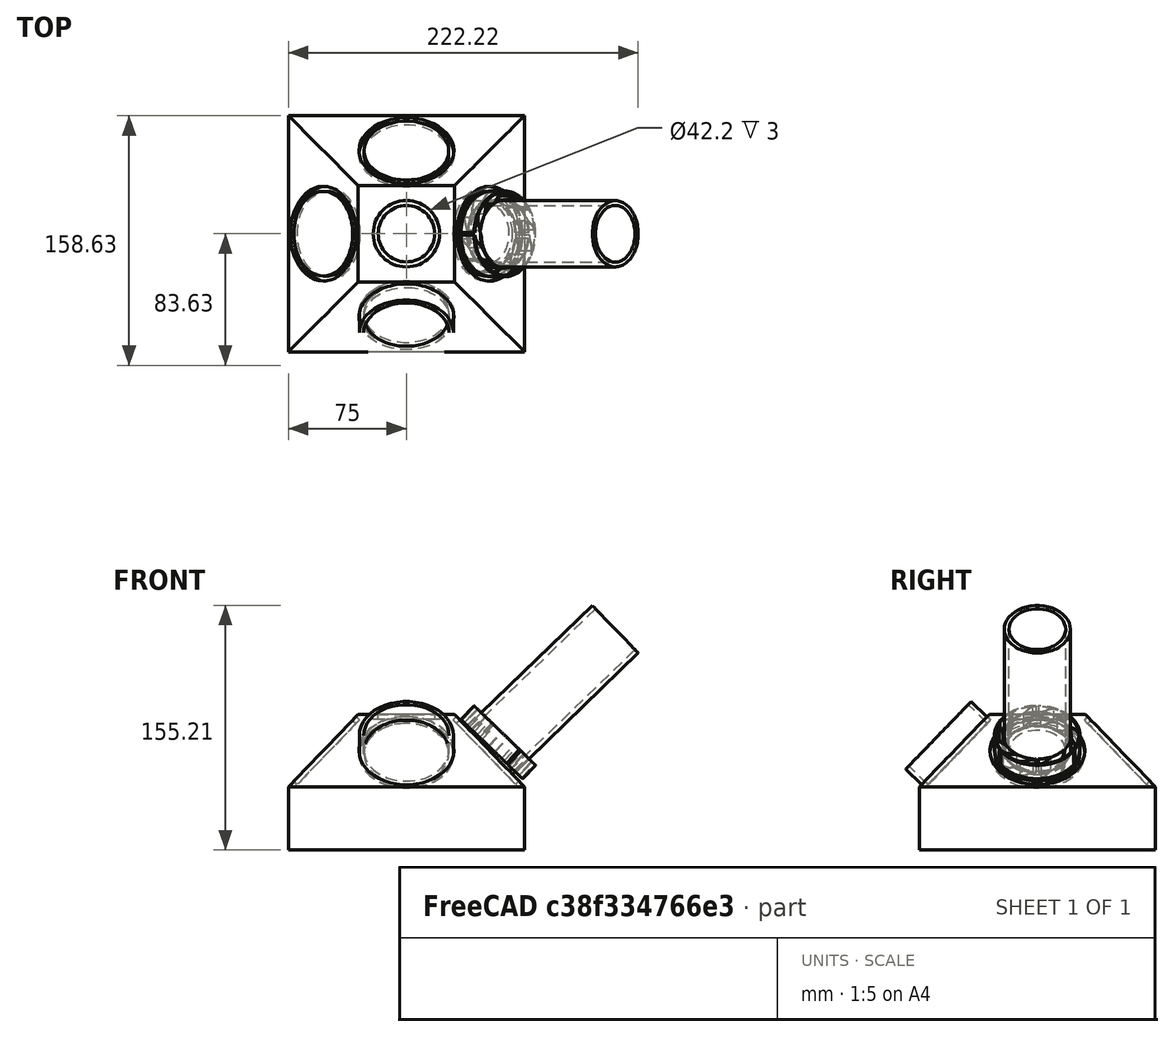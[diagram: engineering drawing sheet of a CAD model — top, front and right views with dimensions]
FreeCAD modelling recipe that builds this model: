
FCSTD DOCUMENT  (FreeCAD 0.21R32867 (Git))
Label: pipestar
License: All rights reserved
LicenseURL: https://en.wikipedia.org/wiki/All_rights_reserved
objects: Sketcher::SketchObject×7, Part::FeaturePython×5, PartDesign::Pocket×4, PartDesign::PolarPattern×4, Mesh::Feature×3, PartDesign::Pad×3, PartDesign::Body×2, Spreadsheet::Sheet×1, App::Part×1
note: 31 computed .brp shape members not serialized (recipe doc carries the construction recipe); baked Part::Feature solids carry a one-line shape summary decoded from their .brp

FEATURE [Mesh::Feature] Mesh
FEATURE [Mesh::Feature] Mesh001
FEATURE [Sketcher::SketchObject] Sketch  label="base1Sketch"
  FullyConstrained = true
  MapMode = 5
  Support = -> [XY_Plane]
  expr: Constraints[9] = <<params>>.baseWidth
  sketch-geometry (4):
    g0: LineSegment StartX=-75 StartY=75 StartZ=0 EndX=75 EndY=75 EndZ=0
    g1: LineSegment StartX=75 StartY=75 StartZ=0 EndX=75 EndY=-75 EndZ=0
    g2: LineSegment StartX=75 StartY=-75 StartZ=0 EndX=-75 EndY=-75 EndZ=0
    g3: LineSegment StartX=-75 StartY=-75 StartZ=0 EndX=-75 EndY=75 EndZ=0
  constraints (11):
    c: Coincident(g0,g1)
    c: Coincident(g1,g2)
    c: Coincident(g2,g3)
    c: Coincident(g3,g0)
    c: Horizontal(g0)
    c: Horizontal(g2)
    c: Vertical(g1)
    c: Vertical(g3)
    c: Equal(g2,g1)
    c: DistanceX(g2,g2) = 150
    c: Symmetric(g1,g0,g-1)
FEATURE [PartDesign::Pad] Pad  label="base1"
  Direction = (0,0,1)
  Length = 40
  Length2 = 10
  Profile = -> Sketch
  ReferenceAxis = -> Sketch [N_Axis]
  Type = 0
  expr: Length = <<params>>.baseHeight1
FEATURE [Sketcher::SketchObject] Sketch001  label="base2Sketch"
  FullyConstrained = true
  MapMode = 5
  Placement = pos=(0,0,40) rot=(0,0,1;0rad)
  Support = -> [Pad]
  expr: Constraints[9] = Sketch.Constraints[9]
  sketch-geometry (4):
    g0: LineSegment StartX=-75 StartY=75 StartZ=0 EndX=75 EndY=75 EndZ=0
    g1: LineSegment StartX=75 StartY=75 StartZ=0 EndX=75 EndY=-75 EndZ=0
    g2: LineSegment StartX=75 StartY=-75 StartZ=0 EndX=-75 EndY=-75 EndZ=0
    g3: LineSegment StartX=-75 StartY=-75 StartZ=0 EndX=-75 EndY=75 EndZ=0
  constraints (11):
    c: Coincident(g0,g1)
    c: Coincident(g1,g2)
    c: Coincident(g2,g3)
    c: Coincident(g3,g0)
    c: Horizontal(g0)
    c: Horizontal(g2)
    c: Vertical(g1)
    c: Vertical(g3)
    c: Equal(g2,g1)
    c: DistanceX(g2,g2) = 150
    c: Symmetric(g1,g0,g-1)
FEATURE [PartDesign::Pad] Pad001  label="base2"
  BaseFeature = -> Pad
  Direction = (0,0,1)
  Length = 46
  Length2 = 10
  Profile = -> Sketch001
  ReferenceAxis = -> Sketch001 [N_Axis]
  TaperAngle = -44
  Type = 0
  expr: Length = <<params>>.baseHeight2
  expr: TaperAngle = <<params>>.baseTaperAngel
FEATURE [Sketcher::SketchObject] Sketch002
  ExternalGeometry = -> [Pad001]
  FullyConstrained = true
  MapMode = 45
  Placement = pos=(-3e-15,-55.9042,59.7743) rot=(0.677258,0.677258,0.287479;3.70145rad)
  Support = -> [Pad001]
  sketch-geometry (4):
    g0: Circle CenterX=4.48428 CenterY=0 CenterZ=0 NormalX=0 NormalY=0 NormalZ=1 AngleXU=0 Radius=30.1
    g1: Circle CenterX=4.48428 CenterY=0 CenterZ=0 NormalX=0 NormalY=0 NormalZ=1 AngleXU=0 Radius=26.9
    g2: LineSegment StartX=-27.4895 StartY=0 StartZ=0 EndX=-25.6157 EndY=0 EndZ=0
    g3: LineSegment StartX=34.5843 StartY=0 StartZ=0 EndX=36.458 EndY=0 EndZ=0
  constraints (13):
    c: Diameter(g0) = 60.2
    c: Coincident(g1,g0)
    c: Diameter(g1) = 53.8
    c: PointOnObject(g0,g-1)
    c: PointOnObject(g2,g-4)
    c: PointOnObject(g2,g0)
    c: PointOnObject(g3,g0)
    c: PointOnObject(g3,g-3)
    c: PointOnObject(g3,g-1)
    c: Perpendicular(g0,g3)
    c: PointOnObject(g2,g-1)
    c: Perpendicular(g0,g2)
    c: Equal(g3,g2)
FEATURE [Sketcher::SketchObject] Sketch003
  FullyConstrained = true
  MapMode = 5
  Placement = pos=(0,0,86) rot=(0,0,1;0rad)
  sketch-geometry (2):
    g0: Circle CenterX=0 CenterY=0 CenterZ=0 NormalX=0 NormalY=0 NormalZ=1 AngleXU=0 Radius=21.1
    g1: Circle CenterX=0 CenterY=0 CenterZ=0 NormalX=0 NormalY=0 NormalZ=1 AngleXU=0 Radius=17.9
  constraints (4):
    c: Coincident(g0,g-1)
    c: Diameter(g0) = 42.2
    c: Coincident(g1,g0)
    c: Diameter(g1) = 35.8
FEATURE [PartDesign::Pocket] Pocket  label="tubeSideMountingRecess"
  BaseFeature = -> Pad001
  Direction = (0,-0.71934,0.694658)
  Length = 3
  Length2 = 5
  Profile = -> Sketch002
  ReferenceAxis = -> Sketch002 [N_Axis]
  Reversed = true
  Type = 0
FEATURE [PartDesign::PolarPattern] PolarPattern
  Angle = 360
  Axis = -> Z_Axis
  BaseFeature = -> Pocket
  Occurrences = 4
  Originals = -> [Pocket]
FEATURE [PartDesign::Pocket] Pocket001  label="tubeTopMountingRecess"
  BaseFeature = -> PolarPattern
  Direction = (0,0,-1)
  Length = 3
  Length2 = 5
  Profile = -> Sketch003
  ReferenceAxis = -> Sketch003 [N_Axis]
  Type = 0
FEATURE [PartDesign::Body] Body  label="base"
  Group = -> [Sketch,Pad,Sketch001,Pad001,Sketch002,Sketch003,Pocket,PolarPattern,Pocket001]
  Origin = -> Origin
  Tip = -> Pocket001
FEATURE [Part::FeaturePython] Tube  label="tubeTop"  # WARN: FeaturePython — macro-defined, semantics opaque (R4)
  AttacherType = Attacher::AttachEngine3D
  Height = 111
  InnerRadius = 18
  OuterRadius = 21
  Placement = pos=(0,0,83) rot=(0,0,1;0rad)
FEATURE [Part::FeaturePython] Tube001  label="tubeSide"  # WARN: FeaturePython — macro-defined, semantics opaque (R4)
  AttacherType = Attacher::AttachEngine3D
  Height = 17
  InnerRadius = 27.1
  OuterRadius = 29.9
  Placement = pos=(153,0,0) rot=(1,0,0;0rad)
FEATURE [Part::FeaturePython] Clone  label="Tube1"  # Draft clone (typed FeaturePython)
  AttacherType = Attacher::AttachEngine3D
  Fuse = false
  Objects = -> [Tube001]
  Placement = pos=(0,-50.63,60.92) rot=(1,0,0;0.802851rad)
  Scale = (1,1,1)
FEATURE [Part::FeaturePython] Array  label="arraySide"  # Draft array (typed FeaturePython)
  AlwaysSyncPlacement = false
  Angle = 360
  ArrayType = 1
  Axis = (0,0,1)
  Base = -> Clone
  Center = (0,0,0)
  Count = 4
  ExpandArray = false
  Fuse = false
  IntervalAxis = (0,0,0)
  IntervalX = (50,0,0)
  IntervalY = (0,50,0)
  IntervalZ = (0,0,50)
  NumberCircles = 3
  NumberPolar = 4
  NumberX = 2
  NumberY = 2
  NumberZ = 1
  PlacementList = 4 placements: [(0,-50.63,60.92),(50.63,-1.42109e-14,60.92),(6.20039e-15,50.63,60.92),(-50.63,1.42109e-14,60.92)]
  RadialDistance = 50
  ScaleList = (4) [(1,1,1),(1,1,1),(1,1,1),(1,1,1)]
  Symmetry = 1
  TangentialDistance = 25
FEATURE [Spreadsheet::Sheet] Spreadsheet  label="params"
  cells = A1=baseWidth; B1(baseWidth)==150 mm; A2=baseHeight1; B2(baseHeight1)==40 mm; A3=baseHeight2; B3(baseHeight2)==46 mm; A4=baseTaperAngel; B4(baseTaperAngel)==-44 °; A6=tubeSideOuterRadius; B6(tubeSideOuterRadius)==60 mm; A7=tubeSideInnerRadius; B7(tubeSideInnerRadius)==54 mm; A8=tubeSideHeight; B8(tubeSideHeight)==14 mm; A10=tubeTopOuterRadius; B10(tubeTopOuterRadius)==42 mm; A11=tubeTopInnerRadius; B11(tubeTopInnerRadius)==36 mm; A12=tubeTopHeight; B12(tubeTopHeight)==108 mm; A14=tubeFittingClearance; B14(tubeFittingClearance)==0.4 mm; A15=tubeMountingRecess; B15(tubeMountingRecess)==3 mm
FEATURE [Sketcher::SketchObject] Sketch004
  FullyConstrained = true
  MapMode = 5
  Support = -> [XY_Plane001]
  sketch-geometry (17):
    g0: LineSegment StartX=0 StartY=0 StartZ=0 EndX=18.0133 EndY=10.4 EndZ=0
    g1: LineSegment StartX=18.0133 StartY=10.4 StartZ=0 EndX=18.7061 EndY=10.8 EndZ=0
    g2: LineSegment StartX=18.7061 StartY=10.8 StartZ=0 EndX=22.8631 EndY=13.2 EndZ=0
    g3: LineSegment StartX=22.8631 StartY=13.2 StartZ=0 EndX=23.5559 EndY=13.6 EndZ=0
    g4: ArcOfCircle CenterX=0 CenterY=0 CenterZ=0 NormalX=0 NormalY=0 NormalZ=1 AngleXU=0 Radius=20.8 StartAngle=0 EndAngle=0.523599
    g5: ArcOfCircle CenterX=0 CenterY=0 CenterZ=0 NormalX=0 NormalY=0 NormalZ=1 AngleXU=0 Radius=27.2 StartAngle=0 EndAngle=0.523599
    g6: ArcOfCircle CenterX=0 CenterY=0 CenterZ=0 NormalX=0 NormalY=0 NormalZ=1 AngleXU=0 Radius=21.6 StartAngle=0 EndAngle=0.408252
    g7: ArcOfCircle CenterX=0 CenterY=0 CenterZ=0 NormalX=0 NormalY=0 NormalZ=1 AngleXU=0 Radius=26.4 StartAngle=0.106675 EndAngle=0.523599
    g8: LineSegment StartX=20.8 StartY=0 StartZ=0 EndX=21.6 EndY=0 EndZ=0
    g9: LineSegment StartX=27.2 StartY=0 StartZ=0 EndX=26.4 EndY=0 EndZ=0
    g10: ArcOfCircle CenterX=28.9052 CenterY=16.6884 CenterZ=0 NormalX=0 NormalY=0 NormalZ=1 AngleXU=0 Radius=11.7768 StartAngle=3.66519 EndAngle=4.19208
    g11: LineSegment StartX=19.8248 StartY=8.57531 StartZ=0 EndX=20.1231 EndY=8.84182 EndZ=0
    g12: ArcOfCircle CenterX=19.3431 CenterY=0 CenterZ=0 NormalX=0 NormalY=0 NormalZ=1 AngleXU=0 Radius=7.45691 StartAngle=0.3865 EndAngle=1.05048
    g13: LineSegment StartX=25.8794 StartY=2.6601 StartZ=0 EndX=26.2499 EndY=2.81088 EndZ=0
    g14: ArcOfCircle CenterX=28.9052 CenterY=16.6884 CenterZ=0 NormalX=0 NormalY=0 NormalZ=1 AngleXU=0 Radius=12.1768 StartAngle=3.87079 EndAngle=4.19208
    g15: ArcOfCircle CenterX=19.3431 CenterY=0 CenterZ=0 NormalX=0 NormalY=0 NormalZ=1 AngleXU=0 Radius=7.05691 StartAngle=0 EndAngle=1.05048
    g16: LineSegment StartX=0 StartY=0 StartZ=0 EndX=22.8514 EndY=6.12303 EndZ=0
  constraints (48):
    c: Coincident(g-1,g0)
    c: Coincident(g0,g1)
    c: Coincident(g1,g2)
    c: Coincident(g2,g3)
    c: Parallel(g3,g2)
    c: Parallel(g2,g1)
    c: Parallel(g1,g0)
    c: Equal(g3,g1)
    c: Coincident(g4,g0)
    c: PointOnObject(g4,g-1)
    c: Coincident(g4,g1)
    c: Coincident(g5,g4)
    c: Coincident(g5,g3)
    c: Coincident(g6,g4)
    c: PointOnObject(g6,g-1)
    c: Coincident(g7,g4)
    c: Coincident(g7,g3)
    c: Coincident(g8,g6)
    c: PointOnObject(g5,g-1)
    c: PointOnObject(g9,g-1)
    c: Coincident(g10,g1)
    c: Equal(g9,g8)
    c: Equal(g8,g1)
    c: DistanceX(g8,g8) = 0.8
    c: Diameter(g5) = 54.4
    c: Diameter(g4) = 41.6
    c: Angle(g4) = 0.523599
    c: Coincident(g11,g6)
    c: PointOnObject(g11,g10)
    c: Perpendicular(g10,g11)
    c: Perpendicular(g10,g1)
    c: Tangent(g12,g10) = 1.5708
    c: Coincident(g13,g7)
    c: Distance(g13) = 0.4
    c: Coincident(g12,g7)
    c: Coincident(g14,g6)
    c: Coincident(g15,g9)
    c: PointOnObject(g13,g15)
    c: Perpendicular(g15,g13)
    c: Coincident(g15,g12)
    c: Tangent(g15,g14) = 1.5708
    c: Coincident(g10,g14)
    c: Perpendicular(g15,g9)
    c: Coincident(g9,g5)
    c: Coincident(g8,g4)
    c: Coincident(g16,g4)
    c: Coincident(g16,g14)
    c: Angle(g-1,g16) = 0.261799
FEATURE [PartDesign::Pad] Pad002
  Direction = (0,0,1)
  Length = 12
  Length2 = 10
  Profile = -> Sketch004
  ReferenceAxis = -> Sketch004 [N_Axis]
  Type = 0
FEATURE [PartDesign::PolarPattern] PolarPattern001
  Angle = 360
  Axis = -> Sketch004 [N_Axis]
  BaseFeature = -> Pad002
  Occurrences = 12
  Originals = -> [Pad002]
FEATURE [Sketcher::SketchObject] Sketch005
  FullyConstrained = false
  MapMode = 5
  Support = -> [XY_Plane001]
  sketch-geometry (4):
    g0: LineSegment StartX=19.6611 StartY=0.75 StartZ=0 EndX=23.4494 EndY=0.75 EndZ=0
    g1: LineSegment StartX=23.4494 StartY=0.75 StartZ=0 EndX=23.4494 EndY=-0.75 EndZ=0
    g2: LineSegment StartX=23.4494 StartY=-0.75 StartZ=0 EndX=19.6611 EndY=-0.75 EndZ=0
    g3: LineSegment StartX=19.6611 StartY=-0.75 StartZ=0 EndX=19.6611 EndY=0.75 EndZ=0
  constraints (9):
    c: Coincident(g0,g1)
    c: Coincident(g1,g2)
    c: Coincident(g2,g3)
    c: Coincident(g3,g0)
    c: Horizontal(g0)
    c: Horizontal(g2)
    c: Vertical(g3)
    c: Symmetric(g1,g0,g-1)
    c: DistanceY(g3,g3) = 1.5
FEATURE [PartDesign::Pocket] Pocket002
  BaseFeature = -> PolarPattern001
  Direction = (0,0,-1)
  Length = 5
  Length2 = 5
  Profile = -> Sketch005
  ReferenceAxis = -> Sketch005 [N_Axis]
  Reversed = true
  Type = 1
FEATURE [PartDesign::PolarPattern] PolarPattern002
  Angle = 360
  Axis = -> Sketch005 [N_Axis]
  BaseFeature = -> Pocket002
  Occurrences = 3
  Originals = -> [Pocket002]
FEATURE [Sketcher::SketchObject] Sketch006
  AttachmentOffset = pos=(0,0,0) rot=(0,0,1;1.0472rad)
  FullyConstrained = false
  MapMode = 5
  Placement = pos=(0,0,0) rot=(0,0,1;1.0472rad)
  Support = -> [XY_Plane001]
  sketch-geometry (4):
    g0: LineSegment StartX=24.6788 StartY=0.75 StartZ=0 EndX=28.7207 EndY=0.75 EndZ=0
    g1: LineSegment StartX=28.7207 StartY=0.75 StartZ=0 EndX=28.7207 EndY=-0.75 EndZ=0
    g2: LineSegment StartX=28.7207 StartY=-0.75 StartZ=0 EndX=24.6788 EndY=-0.75 EndZ=0
    g3: LineSegment StartX=24.6788 StartY=-0.75 StartZ=0 EndX=24.6788 EndY=0.75 EndZ=0
  constraints (9):
    c: Coincident(g0,g1)
    c: Coincident(g1,g2)
    c: Coincident(g2,g3)
    c: Coincident(g3,g0)
    c: Horizontal(g0)
    c: Horizontal(g2)
    c: Vertical(g3)
    c: Symmetric(g1,g0,g-1)
    c: DistanceY(g1,g1) = 1.5
FEATURE [PartDesign::Pocket] Pocket003
  BaseFeature = -> PolarPattern002
  Direction = (0,0,-1)
  Length = 5
  Length2 = 5
  Profile = -> Sketch006
  ReferenceAxis = -> Sketch006 [N_Axis]
  Reversed = true
  Type = 1
FEATURE [PartDesign::PolarPattern] PolarPattern003
  Angle = 360
  Axis = -> Sketch006 [N_Axis]
  BaseFeature = -> Pocket003
  Occurrences = 3
  Originals = -> [Pocket003]
  Refine = true
FEATURE [PartDesign::Body] Body001  label="spacer"
  Group = -> [Sketch004,Pad002,PolarPattern001,Sketch005,Pocket002,PolarPattern002,Sketch006,Pocket003,PolarPattern003]
  Origin = -> Origin001
  Placement = pos=(54.1455,-0.1,64.0361) rot=(0,1,0;0.767945rad)
  Tip = -> PolarPattern003
FEATURE [Part::FeaturePython] Clone001  label="tubeTop-side"  # Draft clone (typed FeaturePython)
  AttacherType = Attacher::AttachEngine3D
  Fuse = false
  Objects = -> [Tube]
  Placement = pos=(52.7892,4.61996e-09,63) rot=(0,1,0;0.802851rad)
  Scale = (1,1,1)
FEATURE [App::Part] Part
  Group = -> [Clone001,Body001,Body,Tube,Clone,Array]
  Origin = -> Origin002
  Placement = pos=(0,-8.8,-81.8) rot=(1,0,0;5.48033rad)
FEATURE [Mesh::Feature] pipstar_complete_transformed  label="pipstar-complete-transformed"
